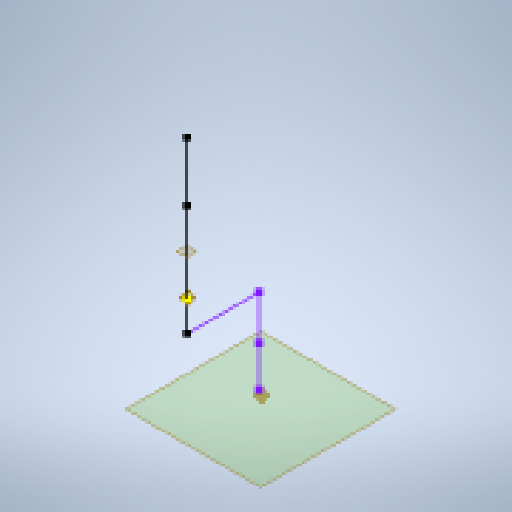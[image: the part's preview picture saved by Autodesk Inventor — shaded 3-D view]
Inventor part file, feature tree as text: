
AUTODESK INVENTOR PART (.ipt)
format: ipt  version: 2025 (Build 290162000, 162)  size: 166,912 bytes
history: native  units: in
note: dims shown in document units (in); Inventor stores cm internally (conversion verified against a paired STEP export)
features: plane x1, other x1, sketch x1
ambient origin geometry x8: Origin, YZ Plane, XZ Plane, XY Plane, X Axis, Y Axis, Z Axis, Center Point
feature tree (3):
  plane  "Work Plane2"
  other  "Work Point2"
  sketch  "3D Sketch1"
